# Revit family: Arper_Aava_trestle-fixed_polypropylene_7604
name_source: partatom
category: Furniture
units: mm (PartAtom-declared; Revit-internal decimal feet)

## family parameters
Always vertical = Yes
Cut with Voids When Loaded = No
OmniClass Number = 23.40.20.00
OmniClass Title = General Furniture and Specialties
Room Calculation Point = No
Shared = No
Work Plane-Based = No

## types (1)
- Arper_Aava_trestle-fixed_polypropylene_7604
    Default Elevation = 0 mm  [stored 0 ft]
    Description = Chair on fixed trestle base in powder-coated aluminium, mounted on 
self-braking castors (of the same colour as the base). Shell in 
polypropylene made with post-consumer recycled materials, mixed 
with virgin material, available in 5 colours. Optional armrests in the 
same colour as the base are also available, equipped with pads in 
polypropylene in the same finish of the shell.
    Manufacturer = ARPER s.p.a.
    Model = Aava 02
    URL = http://www.arper.com

note: [stored X ft] marks values corroborated as IEEE doubles in the binary element streams (Revit-internal decimal feet)
